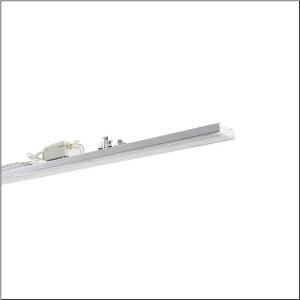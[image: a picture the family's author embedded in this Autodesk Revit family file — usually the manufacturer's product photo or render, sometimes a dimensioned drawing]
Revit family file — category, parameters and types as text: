
# Revit family: licross_r__21_recessed_ho_52tl11dn4dxs_654c
name_source: partatom
category: Lighting Fixtures
units: mm (PartAtom-declared; Revit-internal decimal feet)

## family parameters
Cut with Voids When Loaded = No
Host = Face
Light Source = No
Part Type = Normal
Room Calculation Point = No
Round Connector Dimension = Use Diameter
Shared = No

## types (1)
- --- (1 x LED, 13000 lm, 72.5 W, 4000K)
    Apparent Load = 73 VA
    CIE Flux Codes = 87 95 99 100 100
    Color Rendering = 80
    Color Temperature = 4000K
    Default Elevation = 1800 mm
    Description = Licross® 21 Recessed HO, luminaire insert, of sheet steel, galvanised, coil coated, white, length: 1.500mm, width: 66mm, height: 67mm, LED rated luminous flux: 13.000lm, light colour: 840, control gear: DALI 2, with plug, 5-pole, with phase selection, mains connection: 220..240V, AC, 50/60Hz, rated input power: 73W, halogen-free wiring, primary light control with lens, of plastic, primary optical cover: cover, of PMMA, light emission: direct distribution, primary light characteristic: symmetric, protection rating (complete): IP40, insulation class (complete): insulation class I (protective earthing), certification: CE, ENEC, VDE, UKCA, protection symbol: D if used in an environment without relevant dust loads with corresponding accessories, impact resistance: IK06, permissible ambient temperature for indoor applications: -25..+35°C, corresponds to IFS (International Featured Standards) requirements for safety and quality in the food industry, reducing of maximum allowable ambient temperature of 5°C with ceiling mounting, LABS conformity tested according to VDMA 24364:2018-05, packaging unit: 1 piece
    Height = 58 mm
    Lamp = 1 x LED
    Lamp Light Flux = 13000 lm
    Lamp Power = 72.5 W
    Lamp count = 1
    Length = 1500 mm
    Luminous efficacy = 179 lm/W
    Manufacturer = Siteco
    ModVariant = No
    Model = 52TL11DN4DXS
    Mounting Place = Ceiling
    Mounting Type = Pendant
    Number of Poles = 1
    OnlyDefault = Yes
    Power Factor = 1
    Product Name = Licross® 21 Recessed HO
    Product group = luminaire insert
    ProductGroupID = 901
    Protection Class = Protection class I
    Protection Degree = IP 40
    RLX_Detail_Level = 1
    RLX_Emergency_Light_Flux = 0 lm
    RLX_Emergency_Type = 0
    RLX_Emergency_Type_DB = No
    RlxData = <blob elided: 24569 chars, md5=6e623896>
    Socket = socket
    Standby Power = 0 W
    System Light Flux = 13000 lm
    System Power = 73 W
    Type Comments = factory setting: luminous flux: 100 % | dim-lin: 254 | 415 mA
    Type Image = l_1296930.jpg
    URL = http://relux.com
    VarID = @adj_058823
    Voltage = 0 V
    Weight = 0.00 kg
    Width = 66 mm

## geometry (parser evidence)
native form markers: Blend x4, Sweep x11
no freeform markers — native parametric forms only
